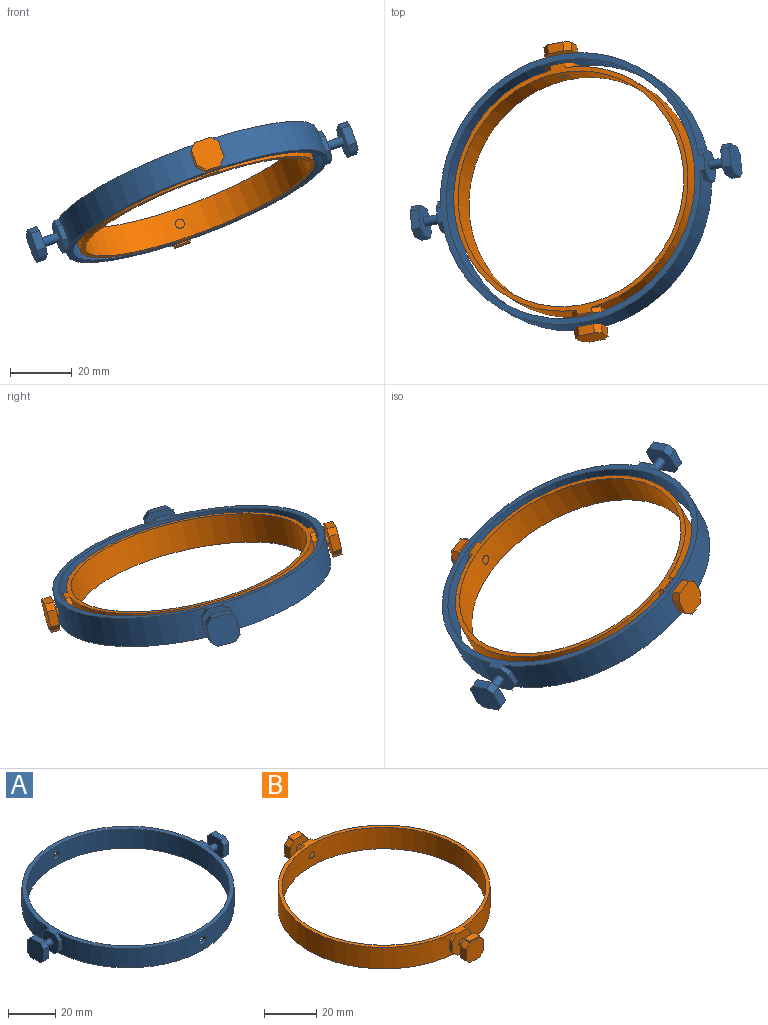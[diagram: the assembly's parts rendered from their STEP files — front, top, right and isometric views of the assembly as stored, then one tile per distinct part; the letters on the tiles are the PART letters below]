
ASSEMBLY  parts=2 mates=1
PART A: 43 faces, bbox 111x90x10 mm
  f0: cylinder r=45mm len=89.86mm, axis (0,0,-1), area 1313.5mm2, adj f3,f4,f5,f22,f23,f24,f38,f39
  f1: cylinder r=45mm len=89.86mm, axis (0,0,-1), area 1313.5mm2, adj f3,f4,f6,f19,f20,f21,f37,f41
  f2: cylinder r=43mm len=86mm, axis (0,0,-1), area 2676.6mm2, adj f3,f4,f5,f6
  f3: plane 93x90mm, normal (0,0,1), area 568.2mm2, adj f0,f1,f2,f18,f19,f22,f36,f37
  f4: plane 93x90mm, normal (0,0,-1), area 568.2mm2, adj f0,f1,f2,f18,f20,f23,f36,f39
  f5: cylinder r=2mm len=4mm, axis (0,-1,0), area 25.1mm2, adj f0,f2
  f6: cylinder r=2mm len=4mm, axis (0,-1,0), area 25.1mm2, adj f1,f2
  f7: plane 10x10mm, normal (-1,0,0), area 92mm2, adj f8,f9,f10,f11,f12,f13,f14,f15
  f8: plane 3x2mm, normal (0,-0.71,-0.71), area 8.5mm2, adj f7,f9,f15,f16
  f9: plane 6x3mm, normal (0,-1,0), area 18mm2, adj f7,f8,f10,f16
  f10: plane 3x2mm, normal (0,-0.71,0.71), area 8.5mm2, adj f7,f9,f11,f16
  f11: plane 6x3mm, normal (0,0,1), area 18mm2, adj f7,f10,f12,f16
  f12: plane 3x2mm, normal (0,0.71,0.71), area 8.5mm2, adj f7,f11,f13,f16
  f13: plane 6x3mm, normal (0,1,0), area 18mm2, adj f7,f12,f14,f16
  f14: plane 3x2mm, normal (0,0.71,-0.71), area 8.5mm2, adj f7,f13,f15,f16
  f15: plane 6x3mm, normal (0,0,-1), area 18mm2, adj f7,f8,f14,f16
  f16: plane 10x10mm, normal (1,0,0), area 84.9mm2, adj f8,f9,f10,f11,f12,f13,f14,f15
  f17: cylinder r=1.5mm len=6mm, axis (1,0,0), area 56.5mm2, adj f16,f18
  f18: plane 10x10mm, normal (-1,0,0), area 80.4mm2, adj f3,f4,f17,f19,f20,f21,f22,f23
  f19: plane 2.5x2.5mm, normal (0,0.71,0.71), area 5.9mm2, adj f1,f3,f18,f21
  f20: plane 2.5x2.5mm, normal (0,0.71,-0.71), area 5.9mm2, adj f1,f4,f18,f21
  f21: plane 5x1.78mm, normal (0,1,0), area 8.9mm2, adj f1,f18,f19,f20
  f22: plane 2.5x2.5mm, normal (0,-0.71,0.71), area 5.9mm2, adj f0,f3,f18,f24
  f23: plane 2.5x2.5mm, normal (0,-0.71,-0.71), area 5.9mm2, adj f0,f4,f18,f24
  f24: plane 5x1.78mm, normal (0,-1,0), area 8.9mm2, adj f0,f18,f22,f23
  f25: plane 10x10mm, normal (1,0,0), area 92mm2, adj f26,f27,f28,f29,f30,f31,f32,f33
  f26: plane 3x2mm, normal (0,0.71,0.71), area 8.5mm2, adj f25,f27,f33,f34
  f27: plane 6x3mm, normal (0,0,1), area 18mm2, adj f25,f26,f28,f34
  f28: plane 3x2mm, normal (0,-0.71,0.71), area 8.5mm2, adj f25,f27,f29,f34
  f29: plane 6x3mm, normal (0,-1,0), area 18mm2, adj f25,f28,f30,f34
  f30: plane 3x2mm, normal (0,-0.71,-0.71), area 8.5mm2, adj f25,f29,f31,f34
  f31: plane 6x3mm, normal (0,0,-1), area 18mm2, adj f25,f30,f32,f34
  f32: plane 3x2mm, normal (0,0.71,-0.71), area 8.5mm2, adj f25,f31,f33,f34
  f33: plane 6x3mm, normal (0,1,0), area 18mm2, adj f25,f26,f32,f34
  f34: plane 10x10mm, normal (-1,0,0), area 84.9mm2, adj f26,f27,f28,f29,f30,f31,f32,f33
  f35: cylinder r=1.5mm len=6mm, axis (-1,0,0), area 56.5mm2, adj f34,f36
  f36: plane 10x10mm, normal (1,0,0), area 80.4mm2, adj f3,f4,f35,f37,f38,f39,f40,f41
  f37: plane 2.5x2.5mm, normal (0,0.71,0.71), area 5.9mm2, adj f1,f3,f36,f42
  f38: plane 2.5x2.5mm, normal (0,-0.71,0.71), area 5.9mm2, adj f0,f3,f36,f40
  f39: plane 2.5x2.5mm, normal (0,-0.71,-0.71), area 5.9mm2, adj f0,f4,f36,f40
  f40: plane 5x1.78mm, normal (0,-1,0), area 8.9mm2, adj f0,f36,f38,f39
  f41: plane 2.5x2.5mm, normal (0,0.71,-0.71), area 5.9mm2, adj f1,f4,f36,f42
  f42: plane 5x1.78mm, normal (0,1,0), area 8.9mm2, adj f1,f36,f37,f41
PART B: 53 faces, bbox 81x98x10 mm
  f0: plane 5.38x0.04mm, normal (0,0,1), area 0.2mm2, adj f15,f17,f19,f49
  f1: cylinder r=40.5mm len=80.85mm, axis (0,0,-1), area 1184.6mm2, adj f5,f6,f25,f26,f27,f40,f41,f42
  f2: cylinder r=40.5mm len=80.85mm, axis (0,0,-1), area 1184.6mm2, adj f5,f6,f22,f23,f24,f39,f43,f44
  f3: cylinder r=1.5mm len=3mm, axis (0,1,0), area 0.3mm2, adj f4,f9
  f4: cylinder r=39mm len=78mm, axis (0,0,-1), area 2436.3mm2, adj f3,f5,f6,f7
  f5: plane 84x81mm, normal (0,0,1), area 389.9mm2, adj f1,f2,f4,f21,f22,f25,f38,f39
  f6: plane 84x81mm, normal (0,0,-1), area 389.9mm2, adj f1,f2,f4,f21,f23,f26,f38,f41
  f7: cylinder r=1.5mm len=3mm, axis (0,1,0), area 0.3mm2, adj f4,f8
  f8: cylinder r=38.97mm len=3mm, axis (0,0,1), area 7.1mm2, adj f7
  f9: cylinder r=38.97mm len=3mm, axis (0,0,1), area 7.1mm2, adj f3
  f10: plane 9.38x9.38mm, normal (0,-1,0), area 80mm2, adj f11,f12,f13,f14,f15,f16,f17,f18
  f11: plane 3x2mm, normal (-0.71,0,-0.71), area 8.5mm2, adj f10,f12,f18,f19
  f12: plane 5.38x3mm, normal (0,0,-1), area 16.1mm2, adj f10,f11,f13,f19
  f13: plane 3x2mm, normal (0.71,0,-0.71), area 8.5mm2, adj f10,f12,f14,f19
  f14: plane 5.38x3mm, normal (1,0,0), area 16.1mm2, adj f10,f13,f15,f19
  f15: plane 3.01x2.01mm, normal (0.71,0,0.71), area 8.5mm2, adj f0,f10,f14,f16,f19,f51
  f16: plane 5.38x0.03mm, normal (0,0,1), area 0.2mm2, adj f10,f15,f17,f52
  f17: plane 3x2.01mm, normal (-0.71,0,0.71), area 8.5mm2, adj f0,f10,f16,f18,f19,f50
  f18: plane 5.38x3mm, normal (-1,0,0), area 16.1mm2, adj f10,f11,f17,f19
  f19: plane 9.38x9.38mm, normal (0,1,0), area 72.9mm2, adj f0,f11,f12,f13,f14,f15,f17,f18
  f20: cylinder r=1.5mm len=4mm, axis (0,1,0), area 37.7mm2, adj f19,f21
  f21: plane 10x10mm, normal (0,-1,0), area 80.4mm2, adj f5,f6,f20,f22,f23,f24,f25,f26
  f22: plane 2.5x2.5mm, normal (-0.71,0,0.71), area 5.9mm2, adj f2,f5,f21,f24
  f23: plane 2.5x2.5mm, normal (-0.71,0,-0.71), area 5.9mm2, adj f2,f6,f21,f24
  f24: plane 5x1.81mm, normal (-1,0,0), area 9mm2, adj f2,f21,f22,f23
  f25: plane 2.5x2.5mm, normal (0.71,0,0.71), area 5.9mm2, adj f1,f5,f21,f27
  f26: plane 2.5x2.5mm, normal (0.71,0,-0.71), area 5.9mm2, adj f1,f6,f21,f27
  f27: plane 5x1.81mm, normal (1,0,0), area 9mm2, adj f1,f21,f25,f26
  f28: plane 10x9.38mm, normal (0,1,0), area 83.3mm2, adj f29,f30,f31,f32,f33,f34,f35,f45
  f29: plane 3x2mm, normal (0.71,0,0.71), area 8.5mm2, adj f28,f30,f36,f47
  f30: plane 5.38x3mm, normal (1,0,0), area 16.1mm2, adj f28,f29,f31,f36
  f31: plane 3x2mm, normal (0.71,0,-0.71), area 8.5mm2, adj f28,f30,f32,f36
  f32: plane 5.38x3mm, normal (0,0,-1), area 16.1mm2, adj f28,f31,f33,f36
  f33: plane 3x2mm, normal (-0.71,0,-0.71), area 8.5mm2, adj f28,f32,f34,f36
  f34: plane 5.38x3mm, normal (-1,0,0), area 16.1mm2, adj f28,f33,f35,f36
  f35: plane 3x2mm, normal (-0.71,0,0.71), area 8.5mm2, adj f28,f34,f36,f46
  f36: plane 10x9.38mm, normal (0,-1,0), area 76.2mm2, adj f29,f30,f31,f32,f33,f34,f35,f37
  f37: cylinder r=1.5mm len=4mm, axis (0,-1,0), area 37.7mm2, adj f36,f38
  f38: plane 10x10mm, normal (0,1,0), area 80.4mm2, adj f5,f6,f37,f39,f40,f41,f42,f43
  f39: plane 2.5x2.5mm, normal (-0.71,0,0.71), area 5.9mm2, adj f2,f5,f38,f44
  f40: plane 2.5x2.5mm, normal (0.71,0,0.71), area 5.9mm2, adj f1,f5,f38,f42
  f41: plane 2.5x2.5mm, normal (0.71,0,-0.71), area 5.9mm2, adj f1,f6,f38,f42
  f42: plane 5x1.81mm, normal (1,0,0), area 9mm2, adj f1,f38,f40,f41
  f43: plane 2.5x2.5mm, normal (-0.71,0,-0.71), area 5.9mm2, adj f2,f6,f38,f44
  f44: plane 5x1.81mm, normal (-1,0,0), area 9mm2, adj f2,f38,f39,f43
  f45: plane 5.38x3mm, normal (0,0,1), area 16.1mm2, adj f28,f36,f46,f47
  f46: plane 3x0.62mm, normal (-1,0,0), area 1.9mm2, adj f28,f35,f36,f45
  f47: plane 3x0.62mm, normal (1,0,0), area 1.9mm2, adj f28,f29,f36,f45
  f48: plane 5.37x2.92mm, normal (0,0,1), area 15.7mm2, adj f49,f50,f51,f52
  f49: plane 5.38x0.62mm, normal (0,1,0), area 3.3mm2, adj f0,f48,f50,f51
  f50: plane 2.93x0.62mm, normal (-1,0,0), area 1.8mm2, adj f17,f48,f49,f52
  f51: plane 2.93x0.63mm, normal (1,0,0), area 1.8mm2, adj f15,f48,f49,f52
  f52: plane 5.38x0.62mm, normal (0,-1,0), area 3.3mm2, adj f16,f48,f50,f51
PLACE A rot(axis=(-0.54,-0.77,0.34),25.5deg) t=(1.16,0.39,-1.15)mm fixed
PLACE B rot(axis=(0.98,0.07,0.17),166.4deg) t=(-2.23,2.39,7.71)mm
MATE slider B.f20 <-> A.f5  axis (0.1,-0.96,0.26) through (-5.15,43.7,-7.88)mm
